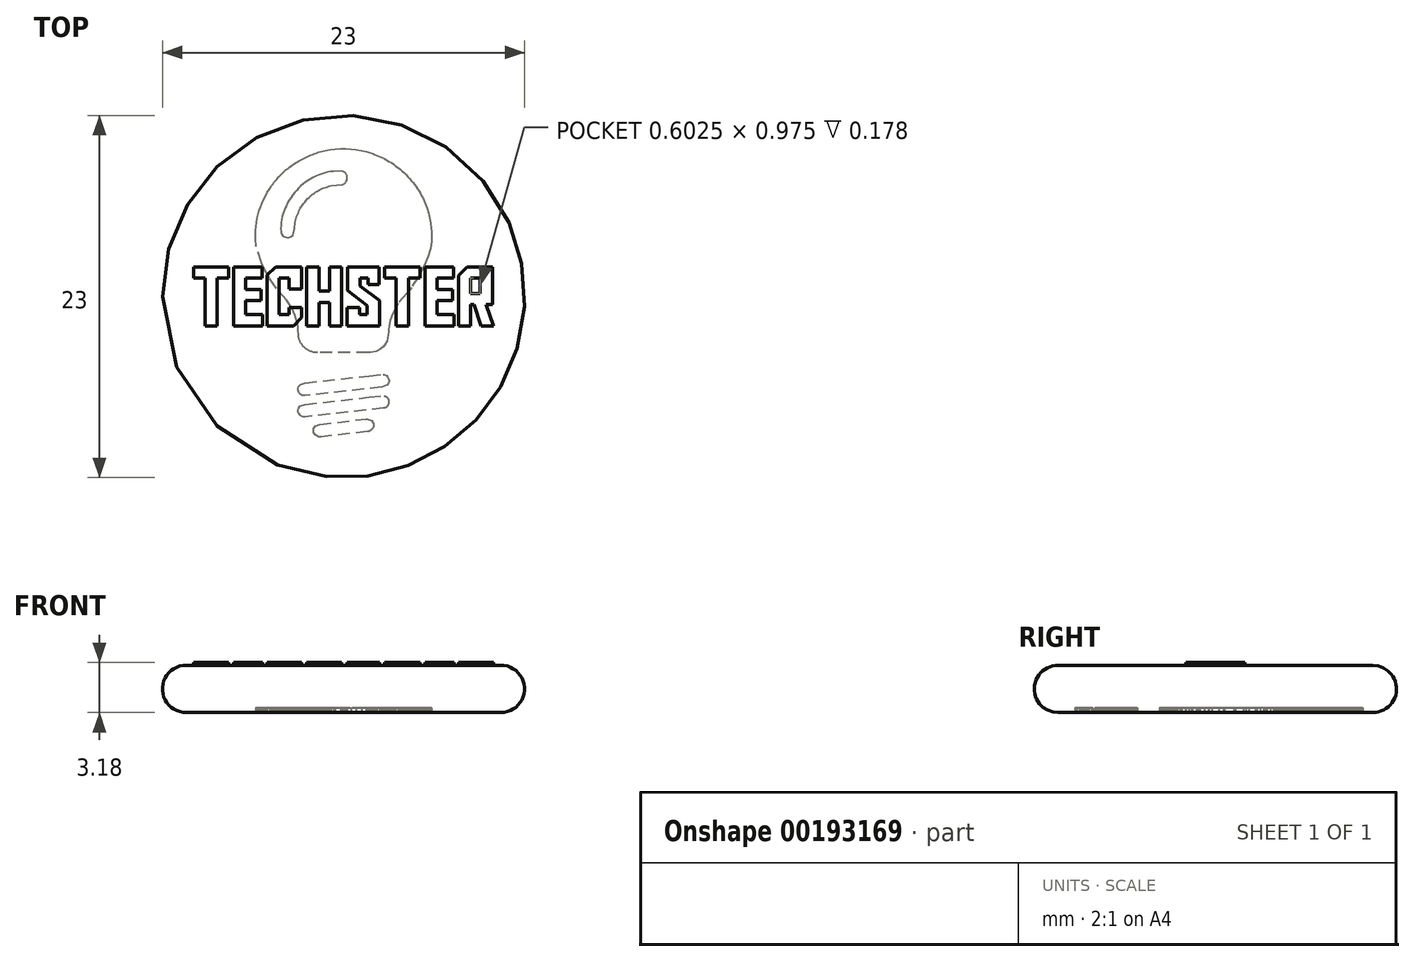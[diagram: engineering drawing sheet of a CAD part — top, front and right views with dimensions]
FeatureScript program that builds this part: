
annotation { "Feature Type Name" : "Feature", "Feature Type Description" : "" }
export const myFeature = defineFeature(function(context is Context, id is Id, definition is map)
    precondition{}
    {
        {
            var Q0;
            Q0=qCreatedBy(makeId("Front.planeOp"),FACE);
            var sketch = newSketch(context, id + "F0", { "sketchPlane" : qUnion([Q0])});
            skLineSegment(sketch, "E0.bottom", {"start": v(0, 0) * mm, "end": v(-10, 0) * mm});
            skLineSegment(sketch, "E0.top", {"start": v(0, 3) * mm, "end": v(-10, 3) * mm});
            skLineSegment(sketch, "E0.left", {"start": v(0, 0) * mm, "end": v(0, 3) * mm});
            skLineSegment(sketch, "E0.right", {"start": v(-10, 0) * mm, "end": v(-10, 3) * mm});
            skArc(sketch, "E1", {"start": v(-10, 3) * mm, "mid": v(-11.5, 1.5) * mm, "end": v(-10, 0) * mm});
            skSolve(sketch);
        }
        {
            var Q0;
            Q0 = qSketchRegion(id + "F0", true);
            var Q1;
            Q1=sQuery(id+"F0.wireOp",EDGE,"E0.left");
            revolve(context, id + "F1", {"entities" : qUnion([Q0]), "axis" : qUnion([Q1]), "revolveType" : RevolveType.FULL});
        }
        {
            var Q0;
            Q0=qCreatedBy(makeId("Top.planeOp"),FACE);
            cPlane(context, id + "F2", {"entities" : qUnion([Q0]), "cplaneType" : CPlaneType.OFFSET, "offset" : 3 * mm, "width" : 152.4 * mm, "height" : 152.4 * mm});
        }
        {
            var Q0;
            Q0=qCreatedBy(id+"F2.planeOp",FACE);
            var sketch = newSketch(context, id + "F3", { "sketchPlane" : qUnion([Q0])});
            skLineSegment(sketch, "E2", {"start": v(-7.3, 1.16) * mm, "end": v(-8.02, 1.16) * mm});
            skLineSegment(sketch, "E3", {"start": v(-8.02, 1.16) * mm, "end": v(-8.02, -1.87) * mm});
            skLineSegment(sketch, "E4", {"start": v(-8.02, -1.87) * mm, "end": v(-8.8, -1.87) * mm});
            skLineSegment(sketch, "E5", {"start": v(-8.8, -1.87) * mm, "end": v(-8.8, 1.16) * mm});
            skLineSegment(sketch, "E6", {"start": v(-8.8, 1.16) * mm, "end": v(-9.54, 1.16) * mm});
            skLineSegment(sketch, "E7", {"start": v(-9.54, 1.16) * mm, "end": v(-9.54, 1.87) * mm});
            skLineSegment(sketch, "E8", {"start": v(-9.54, 1.87) * mm, "end": v(-7.3, 1.87) * mm});
            skLineSegment(sketch, "E9", {"start": v(-7.3, 1.87) * mm, "end": v(-7.3, 1.16) * mm});
            skLineSegment(sketch, "E10", {"start": v(-7, 1.87) * mm, "end": v(-5.18, 1.87) * mm});
            skLineSegment(sketch, "E11", {"start": v(-5.18, 1.87) * mm, "end": v(-5.18, 1.16) * mm});
            skLineSegment(sketch, "E12", {"start": v(-5.18, 1.16) * mm, "end": v(-6.22, 1.16) * mm});
            skLineSegment(sketch, "E13", {"start": v(-6.22, 1.16) * mm, "end": v(-6.22, 0.44) * mm});
            skLineSegment(sketch, "E14", {"start": v(-6.22, 0.44) * mm, "end": v(-5.23, 0.44) * mm});
            skLineSegment(sketch, "E15", {"start": v(-5.23, 0.44) * mm, "end": v(-5.23, -0.26) * mm});
            skLineSegment(sketch, "E16", {"start": v(-5.23, -0.26) * mm, "end": v(-6.2, -0.26) * mm});
            skLineSegment(sketch, "E17", {"start": v(-6.2, -0.26) * mm, "end": v(-6.2, -1.16) * mm});
            skLineSegment(sketch, "E18", {"start": v(-6.2, -1.16) * mm, "end": v(-5.15, -1.16) * mm});
            skLineSegment(sketch, "E19", {"start": v(-5.15, -1.16) * mm, "end": v(-5.15, -1.87) * mm});
            skLineSegment(sketch, "E20", {"start": v(-5.15, -1.87) * mm, "end": v(-7, -1.87) * mm});
            skLineSegment(sketch, "E21", {"start": v(-7, -1.87) * mm, "end": v(-7, 1.87) * mm});
            skLineSegment(sketch, "E22", {"start": v(-3.45, -1.16) * mm, "end": v(-3.45, -0.7) * mm});
            skLineSegment(sketch, "E23", {"start": v(-3.45, -0.7) * mm, "end": v(-2.66, -0.7) * mm});
            skLineSegment(sketch, "E24", {"start": v(-2.66, -0.7) * mm, "end": v(-2.66, -1.35) * mm});
            skLineSegment(sketch, "E25", {"start": v(-2.66, -1.35) * mm, "end": v(-3.18, -1.87) * mm});
            skLineSegment(sketch, "E26", {"start": v(-3.18, -1.87) * mm, "end": v(-4.86, -1.87) * mm});
            skLineSegment(sketch, "E27", {"start": v(-4.86, -1.87) * mm, "end": v(-4.86, 1.36) * mm});
            skLineSegment(sketch, "E28", {"start": v(-4.86, 1.36) * mm, "end": v(-4.3, 1.87) * mm});
            skLineSegment(sketch, "E29", {"start": v(-4.3, 1.87) * mm, "end": v(-2.66, 1.87) * mm});
            skLineSegment(sketch, "E30", {"start": v(-2.66, 1.87) * mm, "end": v(-2.66, 0.46) * mm});
            skLineSegment(sketch, "E31", {"start": v(-2.66, 0.46) * mm, "end": v(-3.45, 0.46) * mm});
            skLineSegment(sketch, "E32", {"start": v(-3.45, 0.46) * mm, "end": v(-3.45, 1.16) * mm});
            skLineSegment(sketch, "E33", {"start": v(-3.45, 1.16) * mm, "end": v(-4.08, 1.16) * mm});
            skLineSegment(sketch, "E34", {"start": v(-4.08, 1.16) * mm, "end": v(-4.08, -1.16) * mm});
            skLineSegment(sketch, "E35", {"start": v(-4.08, -1.16) * mm, "end": v(-3.45, -1.16) * mm});
            skLineSegment(sketch, "E36", {"start": v(-1.56, 0.33) * mm, "end": v(-0.9, 0.33) * mm});
            skLineSegment(sketch, "E37", {"start": v(-0.9, 0.33) * mm, "end": v(-0.9, 1.87) * mm});
            skLineSegment(sketch, "E38", {"start": v(-0.9, 1.87) * mm, "end": v(-0.1, 1.87) * mm});
            skLineSegment(sketch, "E39", {"start": v(-0.1, 1.87) * mm, "end": v(-0.1, -1.87) * mm});
            skLineSegment(sketch, "E40", {"start": v(-0.1, -1.87) * mm, "end": v(-0.9, -1.87) * mm});
            skLineSegment(sketch, "E41", {"start": v(-0.9, -1.87) * mm, "end": v(-0.9, -0.37) * mm});
            skLineSegment(sketch, "E42", {"start": v(-0.9, -0.37) * mm, "end": v(-1.56, -0.37) * mm});
            skLineSegment(sketch, "E43", {"start": v(-1.56, -0.37) * mm, "end": v(-1.56, -1.87) * mm});
            skLineSegment(sketch, "E44", {"start": v(-1.56, -1.87) * mm, "end": v(-2.35, -1.87) * mm});
            skLineSegment(sketch, "E45", {"start": v(-2.35, -1.87) * mm, "end": v(-2.35, 1.87) * mm});
            skLineSegment(sketch, "E46", {"start": v(-2.35, 1.87) * mm, "end": v(-1.56, 1.87) * mm});
            skLineSegment(sketch, "E47", {"start": v(-1.56, 1.87) * mm, "end": v(-1.56, 0.33) * mm});
            skLineSegment(sketch, "E48", {"start": v(2.28, -1.87) * mm, "end": v(0.23, -1.87) * mm});
            skLineSegment(sketch, "E49", {"start": v(0.23, -1.87) * mm, "end": v(0.23, -0.7) * mm});
            skLineSegment(sketch, "E50", {"start": v(0.23, -0.7) * mm, "end": v(1, -0.7) * mm});
            skLineSegment(sketch, "E51", {"start": v(1, -0.7) * mm, "end": v(1, -1.16) * mm});
            skLineSegment(sketch, "E52", {"start": v(1, -1.16) * mm, "end": v(1.5, -1.16) * mm});
            skLineSegment(sketch, "E53", {"start": v(1.5, -1.16) * mm, "end": v(1.5, -0.57) * mm});
            skLineSegment(sketch, "E54", {"start": v(1.5, -0.57) * mm, "end": v(0.25, 0.37) * mm});
            skLineSegment(sketch, "E55", {"start": v(0.25, 0.37) * mm, "end": v(0.25, 1.87) * mm});
            skLineSegment(sketch, "E56", {"start": v(0.25, 1.87) * mm, "end": v(2.26, 1.87) * mm});
            skLineSegment(sketch, "E57", {"start": v(2.26, 1.87) * mm, "end": v(2.26, 0.76) * mm});
            skLineSegment(sketch, "E58", {"start": v(2.26, 0.76) * mm, "end": v(1.55, 0.76) * mm});
            skLineSegment(sketch, "E59", {"start": v(1.55, 0.76) * mm, "end": v(1.55, 1.16) * mm});
            skLineSegment(sketch, "E60", {"start": v(1.55, 1.16) * mm, "end": v(1.04, 1.16) * mm});
            skLineSegment(sketch, "E61", {"start": v(1.04, 1.16) * mm, "end": v(1.04, 0.67) * mm});
            skLineSegment(sketch, "E62", {"start": v(1.04, 0.67) * mm, "end": v(2.28, -0.27) * mm});
            skLineSegment(sketch, "E63", {"start": v(2.28, -0.27) * mm, "end": v(2.28, -1.87) * mm});
            skLineSegment(sketch, "E64", {"start": v(4.85, 1.16) * mm, "end": v(4.14, 1.16) * mm});
            skLineSegment(sketch, "E65", {"start": v(4.14, 1.16) * mm, "end": v(4.14, -1.87) * mm});
            skLineSegment(sketch, "E66", {"start": v(4.14, -1.87) * mm, "end": v(3.35, -1.87) * mm});
            skLineSegment(sketch, "E67", {"start": v(3.35, -1.87) * mm, "end": v(3.35, 1.16) * mm});
            skLineSegment(sketch, "E68", {"start": v(3.35, 1.16) * mm, "end": v(2.62, 1.16) * mm});
            skLineSegment(sketch, "E69", {"start": v(2.62, 1.16) * mm, "end": v(2.62, 1.87) * mm});
            skLineSegment(sketch, "E70", {"start": v(2.62, 1.87) * mm, "end": v(4.85, 1.87) * mm});
            skLineSegment(sketch, "E71", {"start": v(4.85, 1.87) * mm, "end": v(4.85, 1.16) * mm});
            skLineSegment(sketch, "E72", {"start": v(5.17, 1.87) * mm, "end": v(6.98, 1.87) * mm});
            skLineSegment(sketch, "E73", {"start": v(6.98, 1.87) * mm, "end": v(6.98, 1.16) * mm});
            skLineSegment(sketch, "E74", {"start": v(6.98, 1.16) * mm, "end": v(5.94, 1.16) * mm});
            skLineSegment(sketch, "E75", {"start": v(5.94, 1.16) * mm, "end": v(5.94, 0.44) * mm});
            skLineSegment(sketch, "E76", {"start": v(5.94, 0.44) * mm, "end": v(6.93, 0.44) * mm});
            skLineSegment(sketch, "E77", {"start": v(6.93, 0.44) * mm, "end": v(6.93, -0.26) * mm});
            skLineSegment(sketch, "E78", {"start": v(6.93, -0.26) * mm, "end": v(5.95, -0.26) * mm});
            skLineSegment(sketch, "E79", {"start": v(5.95, -0.26) * mm, "end": v(5.95, -1.16) * mm});
            skLineSegment(sketch, "E80", {"start": v(5.95, -1.16) * mm, "end": v(7, -1.16) * mm});
            skLineSegment(sketch, "E81", {"start": v(7, -1.16) * mm, "end": v(7, -1.87) * mm});
            skLineSegment(sketch, "E82", {"start": v(7, -1.87) * mm, "end": v(5.17, -1.87) * mm});
            skLineSegment(sketch, "E83", {"start": v(5.17, -1.87) * mm, "end": v(5.17, 1.87) * mm});
            skLineSegment(sketch, "E84", {"start": v(8.75, -1.87) * mm, "end": v(8.28, -0.52) * mm});
            skLineSegment(sketch, "E85", {"start": v(8.28, -0.52) * mm, "end": v(8.08, -0.52) * mm});
            skLineSegment(sketch, "E86", {"start": v(8.08, -0.52) * mm, "end": v(8.08, -1.87) * mm});
            skLineSegment(sketch, "E87", {"start": v(8.08, -1.87) * mm, "end": v(7.3, -1.87) * mm});
            skLineSegment(sketch, "E88", {"start": v(7.3, -1.87) * mm, "end": v(7.3, 1.34) * mm});
            skLineSegment(sketch, "E89", {"start": v(7.3, 1.34) * mm, "end": v(7.86, 1.87) * mm});
            skLineSegment(sketch, "E90", {"start": v(7.86, 1.87) * mm, "end": v(9.46, 1.87) * mm});
            skLineSegment(sketch, "E91", {"start": v(9.46, 1.87) * mm, "end": v(9.46, -0.5) * mm});
            skLineSegment(sketch, "E92", {"start": v(9.46, -0.5) * mm, "end": v(9.04, -0.5) * mm});
            skLineSegment(sketch, "E93", {"start": v(9.04, -0.5) * mm, "end": v(9.54, -1.87) * mm});
            skLineSegment(sketch, "E94", {"start": v(9.54, -1.87) * mm, "end": v(8.75, -1.87) * mm});
            skLineSegment(sketch, "E95", {"start": v(8.68, 0.18) * mm, "end": v(8.68, 1.16) * mm});
            skLineSegment(sketch, "E96", {"start": v(8.68, 1.16) * mm, "end": v(8.08, 1.16) * mm});
            skLineSegment(sketch, "E97", {"start": v(8.08, 1.16) * mm, "end": v(8.08, 0.18) * mm});
            skLineSegment(sketch, "E98", {"start": v(8.08, 0.18) * mm, "end": v(8.68, 0.18) * mm});
            skSolve(sketch);
        }
        {
            var Q0;
            Q0=qCreatedBy(makeId("Top.planeOp"),FACE);
            var sketch = newSketch(context, id + "F4", { "sketchPlane" : qUnion([Q0])});
            skLineSegment(sketch, "E99", {"start": v(-1.18, 9.26) * mm, "end": v(-0.85, 9.32) * mm});
            skLineSegment(sketch, "E100", {"start": v(-0.85, 9.32) * mm, "end": v(-0.52, 9.36) * mm});
            skLineSegment(sketch, "E101", {"start": v(-0.52, 9.36) * mm, "end": v(-0.19, 9.38) * mm});
            skLineSegment(sketch, "E102", {"start": v(-0.19, 9.38) * mm, "end": v(0.14, 9.38) * mm});
            skLineSegment(sketch, "E103", {"start": v(0.14, 9.38) * mm, "end": v(0.47, 9.36) * mm});
            skLineSegment(sketch, "E104", {"start": v(0.47, 9.36) * mm, "end": v(0.8, 9.32) * mm});
            skLineSegment(sketch, "E105", {"start": v(0.8, 9.32) * mm, "end": v(1.13, 9.27) * mm});
            skLineSegment(sketch, "E106", {"start": v(1.13, 9.27) * mm, "end": v(1.46, 9.2) * mm});
            skLineSegment(sketch, "E107", {"start": v(1.46, 9.2) * mm, "end": v(1.67, 9.13) * mm});
            skLineSegment(sketch, "E108", {"start": v(1.67, 9.13) * mm, "end": v(1.88, 9.06) * mm});
            skLineSegment(sketch, "E109", {"start": v(1.88, 9.06) * mm, "end": v(1.98, 9.02) * mm});
            skLineSegment(sketch, "E110", {"start": v(1.98, 9.02) * mm, "end": v(2.14, 8.96) * mm});
            skLineSegment(sketch, "E111", {"start": v(2.14, 8.96) * mm, "end": v(2.3, 8.9) * mm});
            skLineSegment(sketch, "E112", {"start": v(2.3, 8.9) * mm, "end": v(2.45, 8.82) * mm});
            skLineSegment(sketch, "E113", {"start": v(2.45, 8.82) * mm, "end": v(2.6, 8.74) * mm});
            skLineSegment(sketch, "E114", {"start": v(2.6, 8.74) * mm, "end": v(2.75, 8.66) * mm});
            skLineSegment(sketch, "E115", {"start": v(2.75, 8.66) * mm, "end": v(2.9, 8.58) * mm});
            skLineSegment(sketch, "E116", {"start": v(2.9, 8.58) * mm, "end": v(3.04, 8.49) * mm});
            skLineSegment(sketch, "E117", {"start": v(3.04, 8.49) * mm, "end": v(3.18, 8.4) * mm});
            skLineSegment(sketch, "E118", {"start": v(3.18, 8.4) * mm, "end": v(3.32, 8.3) * mm});
            skLineSegment(sketch, "E119", {"start": v(3.32, 8.3) * mm, "end": v(3.45, 8.2) * mm});
            skLineSegment(sketch, "E120", {"start": v(3.45, 8.2) * mm, "end": v(3.58, 8.09) * mm});
            skLineSegment(sketch, "E121", {"start": v(3.58, 8.09) * mm, "end": v(3.71, 7.98) * mm});
            skLineSegment(sketch, "E122", {"start": v(3.71, 7.98) * mm, "end": v(3.84, 7.86) * mm});
            skLineSegment(sketch, "E123", {"start": v(3.84, 7.86) * mm, "end": v(3.96, 7.74) * mm});
            skLineSegment(sketch, "E124", {"start": v(3.96, 7.74) * mm, "end": v(4.08, 7.62) * mm});
            skLineSegment(sketch, "E125", {"start": v(4.08, 7.62) * mm, "end": v(4.2, 7.5) * mm});
            skLineSegment(sketch, "E126", {"start": v(4.2, 7.5) * mm, "end": v(4.3, 7.37) * mm});
            skLineSegment(sketch, "E127", {"start": v(4.3, 7.37) * mm, "end": v(4.4, 7.24) * mm});
            skLineSegment(sketch, "E128", {"start": v(4.4, 7.24) * mm, "end": v(4.51, 7.1) * mm});
            skLineSegment(sketch, "E129", {"start": v(4.51, 7.1) * mm, "end": v(4.61, 6.97) * mm});
            skLineSegment(sketch, "E130", {"start": v(4.61, 6.97) * mm, "end": v(4.7, 6.83) * mm});
            skLineSegment(sketch, "E131", {"start": v(4.7, 6.83) * mm, "end": v(4.8, 6.68) * mm});
            skLineSegment(sketch, "E132", {"start": v(4.8, 6.68) * mm, "end": v(4.88, 6.54) * mm});
            skLineSegment(sketch, "E133", {"start": v(4.88, 6.54) * mm, "end": v(4.96, 6.39) * mm});
            skLineSegment(sketch, "E134", {"start": v(4.96, 6.39) * mm, "end": v(5.04, 6.24) * mm});
            skLineSegment(sketch, "E135", {"start": v(5.04, 6.24) * mm, "end": v(5.11, 6.09) * mm});
            skLineSegment(sketch, "E136", {"start": v(5.11, 6.09) * mm, "end": v(5.18, 5.93) * mm});
            skLineSegment(sketch, "E137", {"start": v(5.18, 5.93) * mm, "end": v(5.24, 5.77) * mm});
            skLineSegment(sketch, "E138", {"start": v(5.24, 5.77) * mm, "end": v(5.3, 5.61) * mm});
            skLineSegment(sketch, "E139", {"start": v(5.3, 5.61) * mm, "end": v(5.4, 5.3) * mm});
            skLineSegment(sketch, "E140", {"start": v(5.4, 5.3) * mm, "end": v(5.47, 4.99) * mm});
            skLineSegment(sketch, "E141", {"start": v(5.47, 4.99) * mm, "end": v(5.53, 4.67) * mm});
            skLineSegment(sketch, "E142", {"start": v(5.53, 4.67) * mm, "end": v(5.57, 4.34) * mm});
            skLineSegment(sketch, "E143", {"start": v(5.57, 4.34) * mm, "end": v(5.6, 4.13) * mm});
            skLineSegment(sketch, "E144", {"start": v(5.6, 4.13) * mm, "end": v(5.6, 3.91) * mm});
            skLineSegment(sketch, "E145", {"start": v(5.6, 3.91) * mm, "end": v(5.6, 3.7) * mm});
            skLineSegment(sketch, "E146", {"start": v(5.6, 3.7) * mm, "end": v(5.58, 3.48) * mm});
            skLineSegment(sketch, "E147", {"start": v(5.58, 3.48) * mm, "end": v(5.55, 3.26) * mm});
            skLineSegment(sketch, "E148", {"start": v(5.55, 3.26) * mm, "end": v(5.52, 3.05) * mm});
            skLineSegment(sketch, "E149", {"start": v(5.52, 3.05) * mm, "end": v(5.47, 2.84) * mm});
            skLineSegment(sketch, "E150", {"start": v(5.47, 2.84) * mm, "end": v(5.4, 2.63) * mm});
            skLineSegment(sketch, "E151", {"start": v(5.4, 2.63) * mm, "end": v(5.37, 2.53) * mm});
            skLineSegment(sketch, "E152", {"start": v(5.37, 2.53) * mm, "end": v(5.13, 1.93) * mm});
            skLineSegment(sketch, "E153", {"start": v(5.13, 1.93) * mm, "end": v(4.78, 1.27) * mm});
            skLineSegment(sketch, "E154", {"start": v(4.78, 1.27) * mm, "end": v(4.31, 0.58) * mm});
            skLineSegment(sketch, "E155", {"start": v(4.31, 0.58) * mm, "end": v(4.02, 0.21) * mm});
            skLineSegment(sketch, "E156", {"start": v(4.02, 0.21) * mm, "end": v(3.46, -0.46) * mm});
            skLineSegment(sketch, "E157", {"start": v(3.46, -0.46) * mm, "end": v(3.12, -1.1) * mm});
            skLineSegment(sketch, "E158", {"start": v(3.12, -1.1) * mm, "end": v(2.97, -1.54) * mm});
            skLineSegment(sketch, "E159", {"start": v(2.97, -1.54) * mm, "end": v(2.9, -1.87) * mm});
            skLineSegment(sketch, "E160", {"start": v(2.9, -1.87) * mm, "end": v(2.88, -2.13) * mm});
            skLineSegment(sketch, "E161", {"start": v(2.88, -2.13) * mm, "end": v(2.87, -2.27) * mm});
            skLineSegment(sketch, "E162", {"start": v(2.87, -2.27) * mm, "end": v(2.77, -2.84) * mm});
            skLineSegment(sketch, "E163", {"start": v(2.77, -2.84) * mm, "end": v(2.62, -3.1) * mm});
            skLineSegment(sketch, "E164", {"start": v(2.62, -3.1) * mm, "end": v(2.55, -3.18) * mm});
            skLineSegment(sketch, "E165", {"start": v(2.55, -3.18) * mm, "end": v(2.35, -3.35) * mm});
            skLineSegment(sketch, "E166", {"start": v(2.35, -3.35) * mm, "end": v(2.08, -3.5) * mm});
            skLineSegment(sketch, "E167", {"start": v(2.08, -3.5) * mm, "end": v(1.72, -3.57) * mm});
            skLineSegment(sketch, "E168", {"start": v(1.72, -3.57) * mm, "end": v(1.56, -3.58) * mm});
            skLineSegment(sketch, "E169", {"start": v(1.56, -3.58) * mm, "end": v(-1.65, -3.57) * mm});
            skLineSegment(sketch, "E170", {"start": v(-1.65, -3.57) * mm, "end": v(-1.71, -3.57) * mm});
            skLineSegment(sketch, "E171", {"start": v(-1.71, -3.57) * mm, "end": v(-1.78, -3.57) * mm});
            skLineSegment(sketch, "E172", {"start": v(-1.78, -3.57) * mm, "end": v(-1.84, -3.56) * mm});
            skLineSegment(sketch, "E173", {"start": v(-1.84, -3.56) * mm, "end": v(-1.9, -3.55) * mm});
            skLineSegment(sketch, "E174", {"start": v(-1.9, -3.55) * mm, "end": v(-1.97, -3.53) * mm});
            skLineSegment(sketch, "E175", {"start": v(-1.97, -3.53) * mm, "end": v(-2.03, -3.51) * mm});
            skLineSegment(sketch, "E176", {"start": v(-2.03, -3.51) * mm, "end": v(-2.09, -3.5) * mm});
            skLineSegment(sketch, "E177", {"start": v(-2.09, -3.5) * mm, "end": v(-2.15, -3.47) * mm});
            skLineSegment(sketch, "E178", {"start": v(-2.15, -3.47) * mm, "end": v(-2.2, -3.44) * mm});
            skLineSegment(sketch, "E179", {"start": v(-2.2, -3.44) * mm, "end": v(-2.26, -3.4) * mm});
            skLineSegment(sketch, "E180", {"start": v(-2.26, -3.4) * mm, "end": v(-2.32, -3.37) * mm});
            skLineSegment(sketch, "E181", {"start": v(-2.32, -3.37) * mm, "end": v(-2.37, -3.34) * mm});
            skLineSegment(sketch, "E182", {"start": v(-2.37, -3.34) * mm, "end": v(-2.47, -3.26) * mm});
            skLineSegment(sketch, "E183", {"start": v(-2.47, -3.26) * mm, "end": v(-2.51, -3.21) * mm});
            skLineSegment(sketch, "E184", {"start": v(-2.51, -3.21) * mm, "end": v(-2.56, -3.17) * mm});
            skLineSegment(sketch, "E185", {"start": v(-2.56, -3.17) * mm, "end": v(-2.6, -3.12) * mm});
            skLineSegment(sketch, "E186", {"start": v(-2.6, -3.12) * mm, "end": v(-2.64, -3.07) * mm});
            skLineSegment(sketch, "E187", {"start": v(-2.64, -3.07) * mm, "end": v(-2.68, -3.01) * mm});
            skLineSegment(sketch, "E188", {"start": v(-2.68, -3.01) * mm, "end": v(-2.71, -2.96) * mm});
            skLineSegment(sketch, "E189", {"start": v(-2.71, -2.96) * mm, "end": v(-2.74, -2.9) * mm});
            skLineSegment(sketch, "E190", {"start": v(-2.74, -2.9) * mm, "end": v(-2.77, -2.85) * mm});
            skLineSegment(sketch, "E191", {"start": v(-2.77, -2.85) * mm, "end": v(-2.8, -2.79) * mm});
            skLineSegment(sketch, "E192", {"start": v(-2.8, -2.79) * mm, "end": v(-2.82, -2.73) * mm});
            skLineSegment(sketch, "E193", {"start": v(-2.82, -2.73) * mm, "end": v(-2.83, -2.67) * mm});
            skLineSegment(sketch, "E194", {"start": v(-2.83, -2.67) * mm, "end": v(-2.85, -2.6) * mm});
            skLineSegment(sketch, "E195", {"start": v(-2.85, -2.6) * mm, "end": v(-2.86, -2.54) * mm});
            skLineSegment(sketch, "E196", {"start": v(-2.86, -2.54) * mm, "end": v(-2.87, -2.48) * mm});
            skLineSegment(sketch, "E197", {"start": v(-2.87, -2.48) * mm, "end": v(-2.87, -2.41) * mm});
            skLineSegment(sketch, "E198", {"start": v(-2.87, -2.41) * mm, "end": v(-2.87, -2.17) * mm});
            skLineSegment(sketch, "E199", {"start": v(-2.87, -2.17) * mm, "end": v(-2.9, -1.93) * mm});
            skLineSegment(sketch, "E200", {"start": v(-2.9, -1.93) * mm, "end": v(-2.94, -1.69) * mm});
            skLineSegment(sketch, "E201", {"start": v(-2.94, -1.69) * mm, "end": v(-3, -1.45) * mm});
            skLineSegment(sketch, "E202", {"start": v(-3, -1.45) * mm, "end": v(-3.07, -1.22) * mm});
            skLineSegment(sketch, "E203", {"start": v(-3.07, -1.22) * mm, "end": v(-3.17, -1) * mm});
            skLineSegment(sketch, "E204", {"start": v(-3.17, -1) * mm, "end": v(-3.31, -0.7) * mm});
            skLineSegment(sketch, "E205", {"start": v(-3.31, -0.7) * mm, "end": v(-3.48, -0.43) * mm});
            skLineSegment(sketch, "E206", {"start": v(-3.48, -0.43) * mm, "end": v(-3.63, -0.23) * mm});
            skLineSegment(sketch, "E207", {"start": v(-3.63, -0.23) * mm, "end": v(-4.26, 0.51) * mm});
            skLineSegment(sketch, "E208", {"start": v(-4.26, 0.51) * mm, "end": v(-4.7, 1.16) * mm});
            skLineSegment(sketch, "E209", {"start": v(-4.7, 1.16) * mm, "end": v(-5.04, 1.76) * mm});
            skLineSegment(sketch, "E210", {"start": v(-5.04, 1.76) * mm, "end": v(-5.2, 2.11) * mm});
            skLineSegment(sketch, "E211", {"start": v(-5.2, 2.11) * mm, "end": v(-5.54, 3.18) * mm});
            skLineSegment(sketch, "E212", {"start": v(-5.54, 3.18) * mm, "end": v(-5.6, 3.67) * mm});
            skLineSegment(sketch, "E213", {"start": v(-5.6, 3.67) * mm, "end": v(-5.6, 3.93) * mm});
            skLineSegment(sketch, "E214", {"start": v(-5.6, 3.93) * mm, "end": v(-5.59, 4.18) * mm});
            skLineSegment(sketch, "E215", {"start": v(-5.59, 4.18) * mm, "end": v(-5.56, 4.44) * mm});
            skLineSegment(sketch, "E216", {"start": v(-5.56, 4.44) * mm, "end": v(-5.53, 4.7) * mm});
            skLineSegment(sketch, "E217", {"start": v(-5.53, 4.7) * mm, "end": v(-5.48, 4.94) * mm});
            skLineSegment(sketch, "E218", {"start": v(-5.48, 4.94) * mm, "end": v(-5.42, 5.2) * mm});
            skLineSegment(sketch, "E219", {"start": v(-5.42, 5.2) * mm, "end": v(-5.35, 5.44) * mm});
            skLineSegment(sketch, "E220", {"start": v(-5.35, 5.44) * mm, "end": v(-5.27, 5.68) * mm});
            skLineSegment(sketch, "E221", {"start": v(-5.27, 5.68) * mm, "end": v(-5.18, 5.92) * mm});
            skLineSegment(sketch, "E222", {"start": v(-5.18, 5.92) * mm, "end": v(-5.08, 6.16) * mm});
            skLineSegment(sketch, "E223", {"start": v(-5.08, 6.16) * mm, "end": v(-4.96, 6.39) * mm});
            skLineSegment(sketch, "E224", {"start": v(-4.96, 6.39) * mm, "end": v(-4.84, 6.6) * mm});
            skLineSegment(sketch, "E225", {"start": v(-4.84, 6.6) * mm, "end": v(-4.7, 6.83) * mm});
            skLineSegment(sketch, "E226", {"start": v(-4.7, 6.83) * mm, "end": v(-4.56, 7.04) * mm});
            skLineSegment(sketch, "E227", {"start": v(-4.56, 7.04) * mm, "end": v(-4.49, 7.14) * mm});
            skLineSegment(sketch, "E228", {"start": v(-4.49, 7.14) * mm, "end": v(-4.4, 7.25) * mm});
            skLineSegment(sketch, "E229", {"start": v(-4.4, 7.25) * mm, "end": v(-4.31, 7.36) * mm});
            skLineSegment(sketch, "E230", {"start": v(-4.31, 7.36) * mm, "end": v(-4.22, 7.46) * mm});
            skLineSegment(sketch, "E231", {"start": v(-4.22, 7.46) * mm, "end": v(-4.13, 7.57) * mm});
            skLineSegment(sketch, "E232", {"start": v(-4.13, 7.57) * mm, "end": v(-4.04, 7.67) * mm});
            skLineSegment(sketch, "E233", {"start": v(-4.04, 7.67) * mm, "end": v(-3.94, 7.77) * mm});
            skLineSegment(sketch, "E234", {"start": v(-3.94, 7.77) * mm, "end": v(-3.84, 7.86) * mm});
            skLineSegment(sketch, "E235", {"start": v(-3.84, 7.86) * mm, "end": v(-3.74, 7.95) * mm});
            skLineSegment(sketch, "E236", {"start": v(-3.74, 7.95) * mm, "end": v(-3.63, 8.05) * mm});
            skLineSegment(sketch, "E237", {"start": v(-3.63, 8.05) * mm, "end": v(-3.53, 8.13) * mm});
            skLineSegment(sketch, "E238", {"start": v(-3.53, 8.13) * mm, "end": v(-3.42, 8.22) * mm});
            skLineSegment(sketch, "E239", {"start": v(-3.42, 8.22) * mm, "end": v(-3.3, 8.3) * mm});
            skLineSegment(sketch, "E240", {"start": v(-3.3, 8.3) * mm, "end": v(-3.2, 8.38) * mm});
            skLineSegment(sketch, "E241", {"start": v(-3.2, 8.38) * mm, "end": v(-3.08, 8.46) * mm});
            skLineSegment(sketch, "E242", {"start": v(-3.08, 8.46) * mm, "end": v(-2.96, 8.53) * mm});
            skLineSegment(sketch, "E243", {"start": v(-2.96, 8.53) * mm, "end": v(-2.85, 8.6) * mm});
            skLineSegment(sketch, "E244", {"start": v(-2.85, 8.6) * mm, "end": v(-2.73, 8.67) * mm});
            skLineSegment(sketch, "E245", {"start": v(-2.73, 8.67) * mm, "end": v(-2.6, 8.74) * mm});
            skLineSegment(sketch, "E246", {"start": v(-2.6, 8.74) * mm, "end": v(-2.48, 8.8) * mm});
            skLineSegment(sketch, "E247", {"start": v(-2.48, 8.8) * mm, "end": v(-2.36, 8.86) * mm});
            skLineSegment(sketch, "E248", {"start": v(-2.36, 8.86) * mm, "end": v(-2.23, 8.92) * mm});
            skLineSegment(sketch, "E249", {"start": v(-2.23, 8.92) * mm, "end": v(-2.1, 8.97) * mm});
            skLineSegment(sketch, "E250", {"start": v(-2.1, 8.97) * mm, "end": v(-1.97, 9.02) * mm});
            skLineSegment(sketch, "E251", {"start": v(-1.97, 9.02) * mm, "end": v(-1.84, 9.07) * mm});
            skLineSegment(sketch, "E252", {"start": v(-1.84, 9.07) * mm, "end": v(-1.71, 9.12) * mm});
            skLineSegment(sketch, "E253", {"start": v(-1.71, 9.12) * mm, "end": v(-1.58, 9.16) * mm});
            skLineSegment(sketch, "E254", {"start": v(-1.58, 9.16) * mm, "end": v(-1.45, 9.2) * mm});
            skLineSegment(sketch, "E255", {"start": v(-1.45, 9.2) * mm, "end": v(-1.31, 9.23) * mm});
            skLineSegment(sketch, "E256", {"start": v(-1.31, 9.23) * mm, "end": v(-1.18, 9.26) * mm});
            skLineSegment(sketch, "E257", {"start": v(-0.64, 7.94) * mm, "end": v(-0.83, 7.92) * mm});
            skLineSegment(sketch, "E258", {"start": v(-0.83, 7.92) * mm, "end": v(-1.02, 7.89) * mm});
            skLineSegment(sketch, "E259", {"start": v(-1.02, 7.89) * mm, "end": v(-1.21, 7.84) * mm});
            skLineSegment(sketch, "E260", {"start": v(-1.21, 7.84) * mm, "end": v(-1.4, 7.78) * mm});
            skLineSegment(sketch, "E261", {"start": v(-1.4, 7.78) * mm, "end": v(-1.58, 7.72) * mm});
            skLineSegment(sketch, "E262", {"start": v(-1.58, 7.72) * mm, "end": v(-1.75, 7.64) * mm});
            skLineSegment(sketch, "E263", {"start": v(-1.75, 7.64) * mm, "end": v(-1.93, 7.56) * mm});
            skLineSegment(sketch, "E264", {"start": v(-1.93, 7.56) * mm, "end": v(-2.1, 7.46) * mm});
            skLineSegment(sketch, "E265", {"start": v(-2.1, 7.46) * mm, "end": v(-2.26, 7.36) * mm});
            skLineSegment(sketch, "E266", {"start": v(-2.26, 7.36) * mm, "end": v(-2.41, 7.25) * mm});
            skLineSegment(sketch, "E267", {"start": v(-2.41, 7.25) * mm, "end": v(-2.57, 7.13) * mm});
            skLineSegment(sketch, "E268", {"start": v(-2.57, 7.13) * mm, "end": v(-2.71, 7) * mm});
            skLineSegment(sketch, "E269", {"start": v(-2.71, 7) * mm, "end": v(-2.85, 6.88) * mm});
            skLineSegment(sketch, "E270", {"start": v(-2.85, 6.88) * mm, "end": v(-2.99, 6.74) * mm});
            skLineSegment(sketch, "E271", {"start": v(-2.99, 6.74) * mm, "end": v(-3.11, 6.6) * mm});
            skLineSegment(sketch, "E272", {"start": v(-3.11, 6.6) * mm, "end": v(-3.23, 6.44) * mm});
            skLineSegment(sketch, "E273", {"start": v(-3.23, 6.44) * mm, "end": v(-3.34, 6.29) * mm});
            skLineSegment(sketch, "E274", {"start": v(-3.34, 6.29) * mm, "end": v(-3.45, 6.12) * mm});
            skLineSegment(sketch, "E275", {"start": v(-3.45, 6.12) * mm, "end": v(-3.54, 5.96) * mm});
            skLineSegment(sketch, "E276", {"start": v(-3.54, 5.96) * mm, "end": v(-3.63, 5.79) * mm});
            skLineSegment(sketch, "E277", {"start": v(-3.63, 5.79) * mm, "end": v(-3.7, 5.61) * mm});
            skLineSegment(sketch, "E278", {"start": v(-3.7, 5.61) * mm, "end": v(-3.78, 5.43) * mm});
            skLineSegment(sketch, "E279", {"start": v(-3.78, 5.43) * mm, "end": v(-3.84, 5.25) * mm});
            skLineSegment(sketch, "E280", {"start": v(-3.84, 5.25) * mm, "end": v(-3.89, 5.07) * mm});
            skLineSegment(sketch, "E281", {"start": v(-3.89, 5.07) * mm, "end": v(-3.93, 4.88) * mm});
            skLineSegment(sketch, "E282", {"start": v(-3.93, 4.88) * mm, "end": v(-3.96, 4.69) * mm});
            skLineSegment(sketch, "E283", {"start": v(-3.96, 4.69) * mm, "end": v(-3.98, 4.5) * mm});
            skLineSegment(sketch, "E284", {"start": v(-3.98, 4.5) * mm, "end": v(-3.98, 4.3) * mm});
            skLineSegment(sketch, "E285", {"start": v(-3.98, 4.3) * mm, "end": v(-3.98, 4.1) * mm});
            skLineSegment(sketch, "E286", {"start": v(-3.98, 4.1) * mm, "end": v(-3.98, 4.08) * mm});
            skLineSegment(sketch, "E287", {"start": v(-3.98, 4.08) * mm, "end": v(-3.96, 4.02) * mm});
            skLineSegment(sketch, "E288", {"start": v(-3.96, 4.02) * mm, "end": v(-3.92, 3.95) * mm});
            skLineSegment(sketch, "E289", {"start": v(-3.92, 3.95) * mm, "end": v(-3.87, 3.88) * mm});
            skLineSegment(sketch, "E290", {"start": v(-3.87, 3.88) * mm, "end": v(-3.78, 3.8) * mm});
            skLineSegment(sketch, "E291", {"start": v(-3.78, 3.8) * mm, "end": v(-3.68, 3.76) * mm});
            skLineSegment(sketch, "E292", {"start": v(-3.68, 3.76) * mm, "end": v(-3.57, 3.74) * mm});
            skLineSegment(sketch, "E293", {"start": v(-3.57, 3.74) * mm, "end": v(-3.48, 3.74) * mm});
            skLineSegment(sketch, "E294", {"start": v(-3.48, 3.74) * mm, "end": v(-3.4, 3.77) * mm});
            skLineSegment(sketch, "E295", {"start": v(-3.4, 3.77) * mm, "end": v(-3.35, 3.8) * mm});
            skLineSegment(sketch, "E296", {"start": v(-3.35, 3.8) * mm, "end": v(-3.22, 3.9) * mm});
            skLineSegment(sketch, "E297", {"start": v(-3.22, 3.9) * mm, "end": v(-3.1, 4.3) * mm});
            skLineSegment(sketch, "E298", {"start": v(-3.1, 4.3) * mm, "end": v(-3.1, 4.44) * mm});
            skLineSegment(sketch, "E299", {"start": v(-3.1, 4.44) * mm, "end": v(-3.08, 4.57) * mm});
            skLineSegment(sketch, "E300", {"start": v(-3.08, 4.57) * mm, "end": v(-3.06, 4.7) * mm});
            skLineSegment(sketch, "E301", {"start": v(-3.06, 4.7) * mm, "end": v(-3.04, 4.83) * mm});
            skLineSegment(sketch, "E302", {"start": v(-3.04, 4.83) * mm, "end": v(-3, 4.96) * mm});
            skLineSegment(sketch, "E303", {"start": v(-3, 4.96) * mm, "end": v(-2.96, 5.09) * mm});
            skLineSegment(sketch, "E304", {"start": v(-2.96, 5.09) * mm, "end": v(-2.92, 5.21) * mm});
            skLineSegment(sketch, "E305", {"start": v(-2.92, 5.21) * mm, "end": v(-2.87, 5.33) * mm});
            skLineSegment(sketch, "E306", {"start": v(-2.87, 5.33) * mm, "end": v(-2.81, 5.45) * mm});
            skLineSegment(sketch, "E307", {"start": v(-2.81, 5.45) * mm, "end": v(-2.75, 5.57) * mm});
            skLineSegment(sketch, "E308", {"start": v(-2.75, 5.57) * mm, "end": v(-2.68, 5.68) * mm});
            skLineSegment(sketch, "E309", {"start": v(-2.68, 5.68) * mm, "end": v(-2.61, 5.8) * mm});
            skLineSegment(sketch, "E310", {"start": v(-2.61, 5.8) * mm, "end": v(-2.53, 5.9) * mm});
            skLineSegment(sketch, "E311", {"start": v(-2.53, 5.9) * mm, "end": v(-2.45, 6) * mm});
            skLineSegment(sketch, "E312", {"start": v(-2.45, 6) * mm, "end": v(-2.37, 6.1) * mm});
            skLineSegment(sketch, "E313", {"start": v(-2.37, 6.1) * mm, "end": v(-2.28, 6.2) * mm});
            skLineSegment(sketch, "E314", {"start": v(-2.28, 6.2) * mm, "end": v(-2.18, 6.3) * mm});
            skLineSegment(sketch, "E315", {"start": v(-2.18, 6.3) * mm, "end": v(-2.08, 6.38) * mm});
            skLineSegment(sketch, "E316", {"start": v(-2.08, 6.38) * mm, "end": v(-1.98, 6.47) * mm});
            skLineSegment(sketch, "E317", {"start": v(-1.98, 6.47) * mm, "end": v(-1.88, 6.55) * mm});
            skLineSegment(sketch, "E318", {"start": v(-1.88, 6.55) * mm, "end": v(-1.77, 6.62) * mm});
            skLineSegment(sketch, "E319", {"start": v(-1.77, 6.62) * mm, "end": v(-1.66, 6.7) * mm});
            skLineSegment(sketch, "E320", {"start": v(-1.66, 6.7) * mm, "end": v(-1.54, 6.76) * mm});
            skLineSegment(sketch, "E321", {"start": v(-1.54, 6.76) * mm, "end": v(-1.42, 6.82) * mm});
            skLineSegment(sketch, "E322", {"start": v(-1.42, 6.82) * mm, "end": v(-1.3, 6.87) * mm});
            skLineSegment(sketch, "E323", {"start": v(-1.3, 6.87) * mm, "end": v(-1.18, 6.92) * mm});
            skLineSegment(sketch, "E324", {"start": v(-1.18, 6.92) * mm, "end": v(-1.05, 6.96) * mm});
            skLineSegment(sketch, "E325", {"start": v(-1.05, 6.96) * mm, "end": v(-0.93, 7) * mm});
            skLineSegment(sketch, "E326", {"start": v(-0.93, 7) * mm, "end": v(-0.8, 7.03) * mm});
            skLineSegment(sketch, "E327", {"start": v(-0.8, 7.03) * mm, "end": v(-0.08, 7.11) * mm});
            skLineSegment(sketch, "E328", {"start": v(-0.08, 7.11) * mm, "end": v(-0.05, 7.12) * mm});
            skLineSegment(sketch, "E329", {"start": v(-0.05, 7.12) * mm, "end": v(0, 7.14) * mm});
            skLineSegment(sketch, "E330", {"start": v(0, 7.14) * mm, "end": v(0.06, 7.18) * mm});
            skLineSegment(sketch, "E331", {"start": v(0.06, 7.18) * mm, "end": v(0.13, 7.24) * mm});
            skLineSegment(sketch, "E332", {"start": v(0.13, 7.24) * mm, "end": v(0.18, 7.31) * mm});
            skLineSegment(sketch, "E333", {"start": v(0.18, 7.31) * mm, "end": v(0.22, 7.4) * mm});
            skLineSegment(sketch, "E334", {"start": v(0.22, 7.4) * mm, "end": v(0.24, 7.48) * mm});
            skLineSegment(sketch, "E335", {"start": v(0.24, 7.48) * mm, "end": v(0.24, 7.57) * mm});
            skLineSegment(sketch, "E336", {"start": v(0.24, 7.57) * mm, "end": v(0.22, 7.66) * mm});
            skLineSegment(sketch, "E337", {"start": v(0.22, 7.66) * mm, "end": v(0.2, 7.72) * mm});
            skLineSegment(sketch, "E338", {"start": v(0.2, 7.72) * mm, "end": v(0.17, 7.77) * mm});
            skLineSegment(sketch, "E339", {"start": v(0.17, 7.77) * mm, "end": v(0.13, 7.82) * mm});
            skLineSegment(sketch, "E340", {"start": v(0.13, 7.82) * mm, "end": v(0.09, 7.86) * mm});
            skLineSegment(sketch, "E341", {"start": v(0.09, 7.86) * mm, "end": v(0.02, 7.9) * mm});
            skLineSegment(sketch, "E342", {"start": v(0.02, 7.9) * mm, "end": v(-0.08, 7.95) * mm});
            skLineSegment(sketch, "E343", {"start": v(-0.08, 7.95) * mm, "end": v(-0.64, 7.94) * mm});
            skLineSegment(sketch, "E344", {"start": v(1.6, -5.05) * mm, "end": v(2.5, -4.95) * mm});
            skLineSegment(sketch, "E345", {"start": v(2.5, -4.95) * mm, "end": v(2.58, -4.96) * mm});
            skLineSegment(sketch, "E346", {"start": v(2.58, -4.96) * mm, "end": v(2.65, -4.98) * mm});
            skLineSegment(sketch, "E347", {"start": v(2.65, -4.98) * mm, "end": v(2.74, -5.04) * mm});
            skLineSegment(sketch, "E348", {"start": v(2.74, -5.04) * mm, "end": v(2.8, -5.11) * mm});
            skLineSegment(sketch, "E349", {"start": v(2.8, -5.11) * mm, "end": v(2.87, -5.23) * mm});
            skLineSegment(sketch, "E350", {"start": v(2.87, -5.23) * mm, "end": v(2.89, -5.33) * mm});
            skLineSegment(sketch, "E351", {"start": v(2.89, -5.33) * mm, "end": v(2.88, -5.41) * mm});
            skLineSegment(sketch, "E352", {"start": v(2.88, -5.41) * mm, "end": v(2.86, -5.49) * mm});
            skLineSegment(sketch, "E353", {"start": v(2.86, -5.49) * mm, "end": v(2.76, -5.64) * mm});
            skLineSegment(sketch, "E354", {"start": v(2.76, -5.64) * mm, "end": v(2.44, -5.76) * mm});
            skLineSegment(sketch, "E355", {"start": v(2.44, -5.76) * mm, "end": v(-2.44, -6.3) * mm});
            skLineSegment(sketch, "E356", {"start": v(-2.44, -6.3) * mm, "end": v(-2.52, -6.3) * mm});
            skLineSegment(sketch, "E357", {"start": v(-2.52, -6.3) * mm, "end": v(-2.62, -6.28) * mm});
            skLineSegment(sketch, "E358", {"start": v(-2.62, -6.28) * mm, "end": v(-2.73, -6.22) * mm});
            skLineSegment(sketch, "E359", {"start": v(-2.73, -6.22) * mm, "end": v(-2.82, -6.13) * mm});
            skLineSegment(sketch, "E360", {"start": v(-2.82, -6.13) * mm, "end": v(-2.86, -6.04) * mm});
            skLineSegment(sketch, "E361", {"start": v(-2.86, -6.04) * mm, "end": v(-2.89, -5.94) * mm});
            skLineSegment(sketch, "E362", {"start": v(-2.89, -5.94) * mm, "end": v(-2.88, -5.86) * mm});
            skLineSegment(sketch, "E363", {"start": v(-2.88, -5.86) * mm, "end": v(-2.88, -5.84) * mm});
            skLineSegment(sketch, "E364", {"start": v(-2.88, -5.84) * mm, "end": v(-2.84, -5.72) * mm});
            skLineSegment(sketch, "E365", {"start": v(-2.84, -5.72) * mm, "end": v(-2.72, -5.58) * mm});
            skLineSegment(sketch, "E366", {"start": v(-2.72, -5.58) * mm, "end": v(-2.44, -5.5) * mm});
            skLineSegment(sketch, "E367", {"start": v(-2.44, -5.5) * mm, "end": v(1.6, -5.05) * mm});
            skLineSegment(sketch, "E368", {"start": v(1.6, -6.4) * mm, "end": v(2.57, -6.31) * mm});
            skLineSegment(sketch, "E369", {"start": v(2.57, -6.31) * mm, "end": v(2.61, -6.32) * mm});
            skLineSegment(sketch, "E370", {"start": v(2.61, -6.32) * mm, "end": v(2.65, -6.34) * mm});
            skLineSegment(sketch, "E371", {"start": v(2.65, -6.34) * mm, "end": v(2.69, -6.35) * mm});
            skLineSegment(sketch, "E372", {"start": v(2.69, -6.35) * mm, "end": v(2.72, -6.37) * mm});
            skLineSegment(sketch, "E373", {"start": v(2.72, -6.37) * mm, "end": v(2.75, -6.4) * mm});
            skLineSegment(sketch, "E374", {"start": v(2.75, -6.4) * mm, "end": v(2.77, -6.42) * mm});
            skLineSegment(sketch, "E375", {"start": v(2.77, -6.42) * mm, "end": v(2.8, -6.45) * mm});
            skLineSegment(sketch, "E376", {"start": v(2.8, -6.45) * mm, "end": v(2.82, -6.48) * mm});
            skLineSegment(sketch, "E377", {"start": v(2.82, -6.48) * mm, "end": v(2.83, -6.51) * mm});
            skLineSegment(sketch, "E378", {"start": v(2.83, -6.51) * mm, "end": v(2.85, -6.55) * mm});
            skLineSegment(sketch, "E379", {"start": v(2.85, -6.55) * mm, "end": v(2.87, -6.62) * mm});
            skLineSegment(sketch, "E380", {"start": v(2.87, -6.62) * mm, "end": v(2.88, -6.7) * mm});
            skLineSegment(sketch, "E381", {"start": v(2.88, -6.7) * mm, "end": v(2.87, -6.77) * mm});
            skLineSegment(sketch, "E382", {"start": v(2.87, -6.77) * mm, "end": v(2.86, -6.84) * mm});
            skLineSegment(sketch, "E383", {"start": v(2.86, -6.84) * mm, "end": v(2.85, -6.87) * mm});
            skLineSegment(sketch, "E384", {"start": v(2.85, -6.87) * mm, "end": v(2.83, -6.9) * mm});
            skLineSegment(sketch, "E385", {"start": v(2.83, -6.9) * mm, "end": v(2.81, -6.94) * mm});
            skLineSegment(sketch, "E386", {"start": v(2.81, -6.94) * mm, "end": v(2.8, -6.97) * mm});
            skLineSegment(sketch, "E387", {"start": v(2.8, -6.97) * mm, "end": v(2.77, -7) * mm});
            skLineSegment(sketch, "E388", {"start": v(2.77, -7) * mm, "end": v(2.74, -7.02) * mm});
            skLineSegment(sketch, "E389", {"start": v(2.74, -7.02) * mm, "end": v(2.71, -7.04) * mm});
            skLineSegment(sketch, "E390", {"start": v(2.71, -7.04) * mm, "end": v(2.68, -7.06) * mm});
            skLineSegment(sketch, "E391", {"start": v(2.68, -7.06) * mm, "end": v(2.64, -7.08) * mm});
            skLineSegment(sketch, "E392", {"start": v(2.64, -7.08) * mm, "end": v(2.6, -7.09) * mm});
            skLineSegment(sketch, "E393", {"start": v(2.6, -7.09) * mm, "end": v(2.56, -7.1) * mm});
            skLineSegment(sketch, "E394", {"start": v(2.56, -7.1) * mm, "end": v(-2.43, -7.65) * mm});
            skLineSegment(sketch, "E395", {"start": v(-2.43, -7.65) * mm, "end": v(-2.5, -7.66) * mm});
            skLineSegment(sketch, "E396", {"start": v(-2.5, -7.66) * mm, "end": v(-2.55, -7.66) * mm});
            skLineSegment(sketch, "E397", {"start": v(-2.55, -7.66) * mm, "end": v(-2.63, -7.63) * mm});
            skLineSegment(sketch, "E398", {"start": v(-2.63, -7.63) * mm, "end": v(-2.7, -7.6) * mm});
            skLineSegment(sketch, "E399", {"start": v(-2.7, -7.6) * mm, "end": v(-2.77, -7.54) * mm});
            skLineSegment(sketch, "E400", {"start": v(-2.77, -7.54) * mm, "end": v(-2.84, -7.45) * mm});
            skLineSegment(sketch, "E401", {"start": v(-2.84, -7.45) * mm, "end": v(-2.87, -7.37) * mm});
            skLineSegment(sketch, "E402", {"start": v(-2.87, -7.37) * mm, "end": v(-2.89, -7.3) * mm});
            skLineSegment(sketch, "E403", {"start": v(-2.89, -7.3) * mm, "end": v(-2.89, -7.24) * mm});
            skLineSegment(sketch, "E404", {"start": v(-2.89, -7.24) * mm, "end": v(-2.88, -7.18) * mm});
            skLineSegment(sketch, "E405", {"start": v(-2.88, -7.18) * mm, "end": v(-2.86, -7.12) * mm});
            skLineSegment(sketch, "E406", {"start": v(-2.86, -7.12) * mm, "end": v(-2.75, -6.96) * mm});
            skLineSegment(sketch, "E407", {"start": v(-2.75, -6.96) * mm, "end": v(-2.44, -6.85) * mm});
            skLineSegment(sketch, "E408", {"start": v(-2.44, -6.85) * mm, "end": v(1.6, -6.4) * mm});
            skLineSegment(sketch, "E409", {"start": v(-1.53, -8.13) * mm, "end": v(1.43, -7.79) * mm});
            skLineSegment(sketch, "E410", {"start": v(1.43, -7.79) * mm, "end": v(1.5, -7.78) * mm});
            skLineSegment(sketch, "E411", {"start": v(1.5, -7.78) * mm, "end": v(1.77, -7.88) * mm});
            skLineSegment(sketch, "E412", {"start": v(1.77, -7.88) * mm, "end": v(1.88, -8.03) * mm});
            skLineSegment(sketch, "E413", {"start": v(1.88, -8.03) * mm, "end": v(1.9, -8.08) * mm});
            skLineSegment(sketch, "E414", {"start": v(1.9, -8.08) * mm, "end": v(1.91, -8.16) * mm});
            skLineSegment(sketch, "E415", {"start": v(1.91, -8.16) * mm, "end": v(1.9, -8.26) * mm});
            skLineSegment(sketch, "E416", {"start": v(1.9, -8.26) * mm, "end": v(1.87, -8.36) * mm});
            skLineSegment(sketch, "E417", {"start": v(1.87, -8.36) * mm, "end": v(1.8, -8.46) * mm});
            skLineSegment(sketch, "E418", {"start": v(1.8, -8.46) * mm, "end": v(1.7, -8.53) * mm});
            skLineSegment(sketch, "E419", {"start": v(1.7, -8.53) * mm, "end": v(1.61, -8.57) * mm});
            skLineSegment(sketch, "E420", {"start": v(1.61, -8.57) * mm, "end": v(1.54, -8.58) * mm});
            skLineSegment(sketch, "E421", {"start": v(1.54, -8.58) * mm, "end": v(-1.4, -8.92) * mm});
            skLineSegment(sketch, "E422", {"start": v(-1.4, -8.92) * mm, "end": v(-1.57, -8.92) * mm});
            skLineSegment(sketch, "E423", {"start": v(-1.57, -8.92) * mm, "end": v(-1.59, -8.92) * mm});
            skLineSegment(sketch, "E424", {"start": v(-1.59, -8.92) * mm, "end": v(-1.78, -8.8) * mm});
            skLineSegment(sketch, "E425", {"start": v(-1.78, -8.8) * mm, "end": v(-1.9, -8.64) * mm});
            skLineSegment(sketch, "E426", {"start": v(-1.9, -8.64) * mm, "end": v(-1.9, -8.5) * mm});
            skLineSegment(sketch, "E427", {"start": v(-1.9, -8.5) * mm, "end": v(-1.89, -8.4) * mm});
            skLineSegment(sketch, "E428", {"start": v(-1.89, -8.4) * mm, "end": v(-1.76, -8.22) * mm});
            skLineSegment(sketch, "E429", {"start": v(-1.76, -8.22) * mm, "end": v(-1.53, -8.13) * mm});
            skSolve(sketch);
        }
        {
            var Q0;
            Q0 = qSketchRegion(id + "F3", true);
            extrude(context, id + "F5", {"entities" : qUnion([Q0]), "operationType" : NewBodyOperationType.ADD, "depth" : 0.18 * mm});
        }
        {
            var Q0;
            Q0 = qSketchRegion(id + "F4", true);
            extrude(context, id + "F6", {"entities" : qUnion([Q0]), "operationType" : NewBodyOperationType.REMOVE, "depth" : .3 * mm});
        }
    });
